# Revit family: Mixer-Sink-Dorf Vixen1
name_source: partatom
category: Plumbing Fixtures
revit_build: Autodesk Revit 2014 (Build: 20131024_2115(x64)
units: mm (PartAtom-declared; Revit-internal decimal feet)

## types (3) — shared parameters
Assembly Code = D2020300
CW Connection = Yes
CWFU = 1.98
Connector Radius = 10 mm  [stored 0.0328084 ft]
Description = Dorf Vixen Sink Mixer
HW Connection = Yes
HWFU = 1.98
Manufacturer = GWA Bathrooms & Kitchens
Material_ANZRS = Metal-Chrome-Caroma
ModifiedIssue_ANZRS = 20140716 $
Pressure Drop = 0.00 psi
Type Comments = Available in Chrome, Chrome & Black, Chrome & White
URL = http://www.dorf.com.au
Vent Connection = No
WELSRating_ANZRS = WELS 4 Star rated, 7.5L/min
Waste Connection = No
zero-valued in all types: Cost, Default Elevation

## per-type parameters (varying)
| type | Feature | Model |
| Chrome | Metal-Chrome-Caroma | 6494.044A |
| Chrome & Black | Metal-Steel-Powdercoated-Matte Black | 6495.044A |
| Chrome & White | Metal-Steel-Powdercoated-White | 6496.044A |

note: [stored X ft] marks values corroborated as IEEE doubles in the binary element streams (Revit-internal decimal feet)

## geometry (parser evidence)
native form markers: Blend x8, Sweep x1
no freeform markers — native parametric forms only
